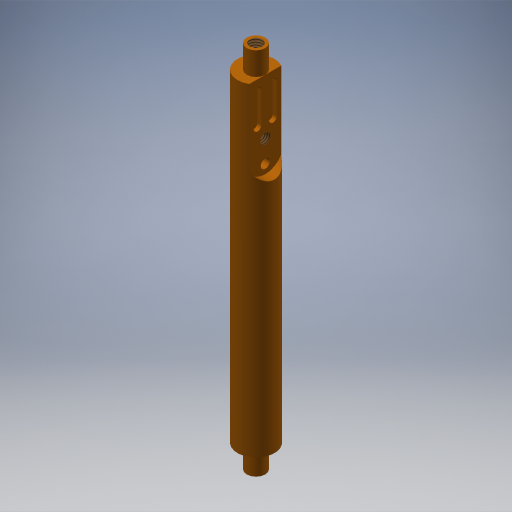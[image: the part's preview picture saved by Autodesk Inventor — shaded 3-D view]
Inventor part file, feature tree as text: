
AUTODESK INVENTOR PART (.ipt)
format: ipt  version: 2024.3 (Build 283343000, 343)  size: 327,680 bytes
history: native  units: mm
features: sketch x8, extrude x5, hole x4, plane x1
ambient origin geometry x8: Origin, YZ Plane, XZ Plane, XY Plane, X Axis, Y Axis, Z Axis, Center Point
bodies: Volumenkörper1 (feature_tree)
feature tree (18):
  extrude  "Extrusion1"  Depth=120.0mm TaperAngle=0.0deg
  extrude  "Extrusion2"  Depth=7.5mm TaperAngle=0.0deg
  extrude  "Extrusion3"  Depth=10.0mm
  hole  "Bohrung1"  [1 undecoded]
  hole  "Bohrung2"  [1 undecoded]
  plane  "Arbeitsebene1"
  extrude  "Extrusion4"  Depth=10.0mm
  extrude  "Extrusion5"  Depth=10.0mm
  hole  "Bohrung3"  [1 undecoded]
  hole  "Bohrung4"  [1 undecoded]
  sketch  "Skizze2"  dims[d0=12.0mm d1=120.0mm d2=0.0mm]
  sketch  "Skizze3"  dims[d3=6.0mm d4=7.5mm d5=0.0mm]
  sketch  "Skizze4"  dims[d6=7.5mm d7=0.0mm]
  sketch  "Skizze5"  dims[d8=4.134mm d9=10.0mm d10=4.0mm d11=2.0mm d12=90.0deg d13=14.2mm d14=20.594885mm]
  sketch  "Skizze7"  dims[d15=4.134mm d16=10.0mm d17=4.0mm d18=2.0mm d19=90.0deg d20=14.2mm d21=20.594885mm d22=22.0mm]
  sketch  "Skizze8"  dims[d23=3.0mm d24=0.0mm d25=5.0mm]
  sketch  "Skizze9"  dims[d26=2.5mm d27=2.5mm]
  sketch  "Skizze10"  dims[d28=3.5mm d29=3.5mm d30=10.0mm d31=10.0mm d32=1.3mm d33=0.0mm d34=18.0mm d35=3.242mm d36=8.0mm d37=4.0mm d38=2.0mm d39=90.0deg d40=11.8mm d41=20.594885mm d42=7.0mm d43=3.0mm d44=8.0mm d45=4.0mm d46=2.0mm d47=90.0deg d48=11.8mm d49=20.594885mm]
note: 4 required parameter values undecoded (feature->parameter linkage not recoverable at this tier; creation-order binding heuristic only, values carry confidence <= 0.55)
